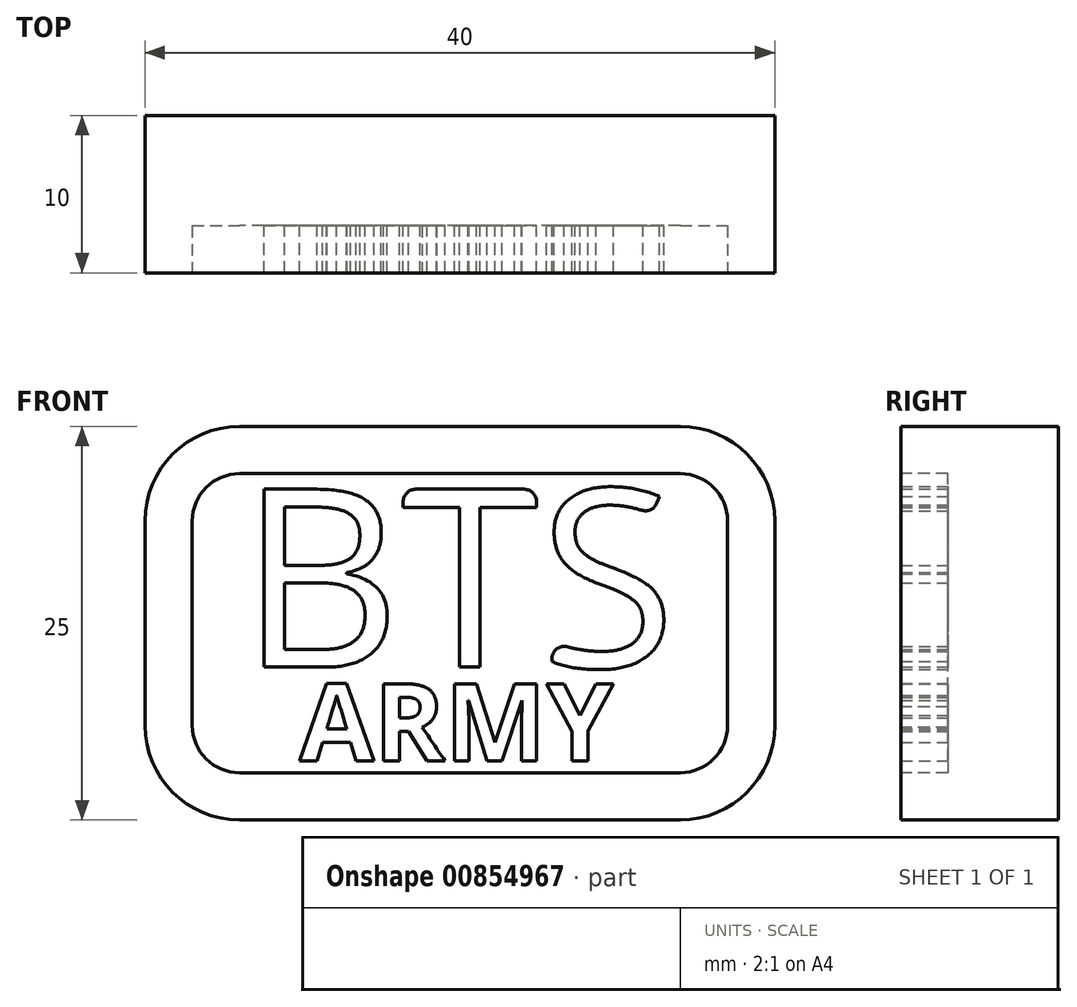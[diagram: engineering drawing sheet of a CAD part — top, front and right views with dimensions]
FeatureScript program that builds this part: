
annotation { "Feature Type Name" : "Feature", "Feature Type Description" : "" }
export const myFeature = defineFeature(function(context is Context, id is Id, definition is map)
    precondition{}
    {
        {
            var Q0;
            Q0=qCreatedBy(makeId("Front.planeOp"),FACE);
            var sketch = newSketch(context, id + "F0", { "sketchPlane" : qUnion([Q0])});
            skLineSegment(sketch, "E0.bottom", {"start": v(20, -12.5) * mm, "end": v(-20, -12.5) * mm});
            skLineSegment(sketch, "E0.top", {"start": v(20, 12.5) * mm, "end": v(-20, 12.5) * mm});
            skLineSegment(sketch, "E0.left", {"start": v(20, -12.5) * mm, "end": v(20, 12.5) * mm});
            skLineSegment(sketch, "E0.right", {"start": v(-20, -12.5) * mm, "end": v(-20, 12.5) * mm});
            skPoint(sketch, "E0.middle", {"position": v(0, 0) * mm});
            skSolve(sketch);
        }
        {
            var Q0;
            Q0=makeQuery(id+"F0.imprint","IMPRINT",FACE,{"disambiguationData":[TD([[makeQuery(id+"F0.imprint","IMPRINT",EDGE,{"derivedFrom":sQuery(id+"F0.wireOp",EDGE,"E0.bottom")}),-1.0]])]});
            extrude(context, id + "F1", {"entities" : qUnion([Q0]), "endBound" : BoundingType.SYMMETRIC, "depth" : 10 * mm, "offsetDistance" : 25 * mm});
        }
        {
            var Q0;
            Q0=makeQuery(id+"F1.opExtrude","SWEPT_EDGE",EDGE,{"disambiguationData":[OSD([sQuery(id+"F0.wireOp",EDGE,"E0.top"),sQuery(id+"F0.wireOp",EDGE,"E0.right")])]});
            var Q1;
            Q1=makeQuery(id+"F1.opExtrude","SWEPT_EDGE",EDGE,{"disambiguationData":[OSD([sQuery(id+"F0.wireOp",EDGE,"E0.bottom"),sQuery(id+"F0.wireOp",EDGE,"E0.right")])]});
            var Q2;
            Q2=makeQuery(id+"F1.opExtrude","SWEPT_EDGE",EDGE,{"disambiguationData":[OSD([sQuery(id+"F0.wireOp",EDGE,"E0.bottom"),sQuery(id+"F0.wireOp",EDGE,"E0.left")])]});
            var Q3;
            Q3=makeQuery(id+"F1.opExtrude","SWEPT_EDGE",EDGE,{"disambiguationData":[OSD([sQuery(id+"F0.wireOp",EDGE,"E0.top"),sQuery(id+"F0.wireOp",EDGE,"E0.left")])]});
            fillet(context, id + "F2", {"entities" : qUnion([Q0, Q1, Q2, Q3]), "radius" : 6 * mm, "tangentPropagation" : true, "allowEdgeOverflow" : false});
        }
        {
            var Q0;
            Q0=makeQuery(id+"F1.opExtrude","CAP_FACE",FACE,{"disambiguationData":[OSD([sQuery(id+"F0.wireOp",EDGE,"E0.bottom"),sQuery(id+"F0.wireOp",EDGE,"E0.top"),sQuery(id+"F0.wireOp",EDGE,"E0.left"),sQuery(id+"F0.wireOp",EDGE,"E0.right")])],"isStart":false});
            var sketch = newSketch(context, id + "F3", { "sketchPlane" : qUnion([Q0])});
            skLineSegment(sketch, "E1.bottom", {"start": v(17, -9.5) * mm, "end": v(-17, -9.5) * mm});
            skLineSegment(sketch, "E1.top", {"start": v(17, 9.5) * mm, "end": v(-17, 9.5) * mm});
            skLineSegment(sketch, "E1.left", {"start": v(17, -9.5) * mm, "end": v(17, 9.5) * mm});
            skLineSegment(sketch, "E1.right", {"start": v(-17, -9.5) * mm, "end": v(-17, 9.5) * mm});
            skPoint(sketch, "E1.middle", {"position": v(0, 0) * mm});
            skSolve(sketch);
        }
        {
            var Q0;
            Q0=makeQuery(id+"F3.imprint","IMPRINT",FACE,{"disambiguationData":[TD([[makeQuery(id+"F3.imprint","IMPRINT",EDGE,{"derivedFrom":sQuery(id+"F3.wireOp",EDGE,"E1.bottom")}),-1.0]])]});
            extrude(context, id + "F4", {"entities" : qUnion([Q0]), "operationType" : NewBodyOperationType.REMOVE, "oppositeDirection" : true, "depth" : 3 * mm, "offsetDistance" : 25 * mm});
        }
        {
            var Q0;
            Q0=makeQuery(id+"F4.boolean.opBoolean","COPY",EDGE,{"derivedFrom":makeQuery(id+"F4.opExtrude","SWEPT_EDGE",EDGE,{"disambiguationData":[OSD([sQuery(id+"F3.wireOp",EDGE,"E1.top"),sQuery(id+"F3.wireOp",EDGE,"E1.right")])]})});
            var Q1;
            Q1=makeQuery(id+"F4.boolean.opBoolean","COPY",EDGE,{"derivedFrom":makeQuery(id+"F4.opExtrude","SWEPT_EDGE",EDGE,{"disambiguationData":[OSD([sQuery(id+"F3.wireOp",EDGE,"E1.top"),sQuery(id+"F3.wireOp",EDGE,"E1.left")])]})});
            var Q2;
            Q2=makeQuery(id+"F4.boolean.opBoolean","COPY",EDGE,{"derivedFrom":makeQuery(id+"F4.opExtrude","SWEPT_EDGE",EDGE,{"disambiguationData":[OSD([sQuery(id+"F3.wireOp",EDGE,"E1.bottom"),sQuery(id+"F3.wireOp",EDGE,"E1.left")])]})});
            var Q3;
            Q3=makeQuery(id+"F4.boolean.opBoolean","COPY",EDGE,{"derivedFrom":makeQuery(id+"F4.opExtrude","SWEPT_EDGE",EDGE,{"disambiguationData":[OSD([sQuery(id+"F3.wireOp",EDGE,"E1.bottom"),sQuery(id+"F3.wireOp",EDGE,"E1.right")])]})});
            fillet(context, id + "F5", {"entities" : qUnion([Q0, Q1, Q2, Q3]), "radius" : 3 * mm, "tangentPropagation" : true, "allowEdgeOverflow" : false});
        }
        {
            var Q0;
            Q0=makeQuery(id+"F4.boolean.opBoolean","COPY",FACE,{"derivedFrom":makeQuery(id+"F4.opExtrude","CAP_FACE",FACE,{"disambiguationData":[OSD([sQuery(id+"F3.wireOp",EDGE,"E1.bottom"),sQuery(id+"F3.wireOp",EDGE,"E1.top"),sQuery(id+"F3.wireOp",EDGE,"E1.left"),sQuery(id+"F3.wireOp",EDGE,"E1.right")])],"isStart":false})});
            var sketch = newSketch(context, id + "F6", { "sketchPlane" : qUnion([Q0])});
            skText(sketch, "E2", { "text": "BTS\n", "fontName": "OpenSans-Regular.ttf"});
            skPoint(sketch, "E2.firstSnap0", {"position": v(-16.12, 8.62) * mm});
            const initialGuessF6  = {"E2": [-0.014, -0.00279, 1, 0, 0.0114]};
            skSetInitialGuess(sketch, initialGuessF6);
            skSolve(sketch);
        }
        {
            var Q0;
            Q0 = qSketchRegion(id + "F6", true);
            extrude(context, id + "F7", {"entities" : qUnion([Q0]), "operationType" : NewBodyOperationType.ADD, "depth" : 3 * mm, "offsetDistance" : 25 * mm});
        }
        {
            var Q0;
            Q0=makeQuery(id+"F7.opExtrude","SWEPT_EDGE",EDGE,{"disambiguationData":[OSD([sQuery(id+"F6.wireOp",EDGE,"E2.sketch_text.stroke-28"),sQuery(id+"F6.wireOp",EDGE,"E2.sketch_text.stroke-29")])]});
            var Q1;
            Q1=makeQuery(id+"F7.opExtrude","SWEPT_EDGE",EDGE,{"disambiguationData":[OSD([sQuery(id+"F6.wireOp",EDGE,"E2.sketch_text.stroke-29"),sQuery(id+"F6.wireOp",EDGE,"E2.sketch_text.stroke-30")])]});
            var Q2;
            Q2=makeQuery(id+"F7.opExtrude","SWEPT_EDGE",EDGE,{"disambiguationData":[OSD([sQuery(id+"F6.wireOp",EDGE,"E2.sketch_text.stroke-36"),sQuery(id+"F6.wireOp",EDGE,"E2.sketch_text.stroke-37")])]});
            var Q3;
            Q3=makeQuery(id+"F7.opExtrude","SWEPT_EDGE",EDGE,{"disambiguationData":[OSD([sQuery(id+"F6.wireOp",EDGE,"E2.sketch_text.stroke-49"),sQuery(id+"F6.wireOp",EDGE,"E2.sketch_text.stroke-50")])]});
            fillet(context, id + "F8", {"entities" : qUnion([Q0, Q1, Q2, Q3]), "radius" : 0.8 * mm, "tangentPropagation" : true, "allowEdgeOverflow" : false});
        }
        {
            var Q0;
            {var subQ0=sQuery(id+"F3.wireOp",EDGE,"E1.right");var subQ1=sQuery(id+"F3.wireOp",EDGE,"E1.top");var subQ2=sQuery(id+"F3.wireOp",EDGE,"E1.left");var subQ3=sQuery(id+"F3.wireOp",EDGE,"E1.bottom");Q0=makeQuery(id+"F7.boolean.opBoolean","SPLIT",FACE,{"disambiguationData":[TD([makeQuery(id+"F4.boolean.opBoolean","COPY",FACE,{"derivedFrom":makeQuery(id+"F4.opExtrude","SWEPT_FACE",FACE,{"disambiguationData":[OSD([subQ3])]})})])],"derivedFrom":makeQuery(id+"F4.boolean.opBoolean","COPY",FACE,{"derivedFrom":makeQuery(id+"F4.opExtrude","CAP_FACE",FACE,{"disambiguationData":[OSD([subQ3,subQ1,subQ2,subQ0])],"isStart":false})})});}
            var sketch = newSketch(context, id + "F9", { "sketchPlane" : qUnion([Q0])});
            skPoint(sketch, "E3", {"position": v(-10.18, -9.5) * mm});
            skPoint(sketch, "E4.MirrorP", {"position": v(10.18, -9.5) * mm});
            skText(sketch, "E5", { "text": "ARMY", "fontName": "OpenSans-Bold.ttf"});
            const initialGuessF9  = {"E5": [-0.01018, -0.00873, 1, 0, 0.00492]};
            skSetInitialGuess(sketch, initialGuessF9);
            skSolve(sketch);
        }
        {
            var Q0;
            Q0 = qSketchRegion(id + "F9", true);
            extrude(context, id + "F10", {"entities" : qUnion([Q0]), "operationType" : NewBodyOperationType.ADD, "depth" : 3 * mm, "offsetDistance" : 25 * mm});
        }
    });
